# Revit family: P400269-009
name_source: partatom
category: Lighting Fixtures
units: mm (PartAtom-declared; Revit-internal decimal feet)

## family parameters
Cut with Voids When Loaded = No
Host = Face
Light Source = No
OmniClass Number = 23.80.70.11.14.17
OmniClass Title = Direct/Indirect
Part Type = Normal
Room Calculation Point = No
Round Connector Dimension = Use Diameter
Shared = Yes

## types (1)
- P400269-009
    Apparent Load = 60 VA
    Assembly Code = D5020200
    Connector Description = Lighting Connector
    Default Elevation = 48 "
    Description = Mill Beam Collection Six-Light Brushed Nickel/Faux Concrete Industrial Style Linear Island Chandelier
    Features = Give an unexpected artisanal edginess with the Mill Beam Collection 6-Light Brushed Nickel Industrial Linear Island Chandelier Light. The slab silhouette is coated in a faux concrete finish accented by brushed nickel stems and ceiling plate to create the perfect blend of organic and industrial character to create the perfect blend of organic and industrial character.
Application: Give an unexpected artisanal edginess with the Mill Beam Collection 6-Light Brushed Nickel Industrial Linear Island Chandelier Light ideal for any kitchen island or dining room.
Styles: Perfect for urban industrial and farmhouse style settings.
Finish: The slab silhouette is coated in a faux concrete finish accented by brushed nickel stems and ceiling plate to create the perfect blend of organic and industrial character.
Materials: Constructed from steel to ensure a long product lifespan
mount the light fixture horizontally or vertically.
Glass/Shades: We recommend using vintage bulbs to enhance the light fixture's rustic aesthetic.
Bulbs: For ideal illumination, use 6 medium base bulbs that are sold separately (60w max - LED/CFL/incandescent). Compatible with dimmable bulbs.
Dimensions: Measures 48-inch length by 2-3/8-inch height by 2-3/4-inch depth.
Certifications: cETLus Damp Location Listed.
Pairs With: Pairs with the Hemsworth, Bonn, and Foster collections by Progress Lighting.
Warranty: Our 1-Year Limited Warranty guarantees your complete satisfaction with your purchase and includes professional after-sales customer service support.
    Fixture distribution = Direct
    Glass = Paint - Hubbell - White Texture
    Gold = Hubbell - Gold
    Housing Material = Paint - Hubbell - Light Silver
    Lamp = LED/CFL/incandescent
    Load Classification = Lighting
    Manufacturer = Progress Lighting
    Model = P400269-009
    Power Factor = 1
    Product Documentation Link = https://hubbellcdn.com
    Product Link = https://www.hubbell.com
    Support = Paint- Hubbell - Gray
    URL = https://www.hubbell.com
    Voltage = 120 V
    Warranty = 1 year Warranty
    Wattage Comments = 60W
    Watts = 60 W
    Width = 7.5 "

## geometry (parser evidence)
native form markers: Sweep x5
no freeform markers — native parametric forms only
